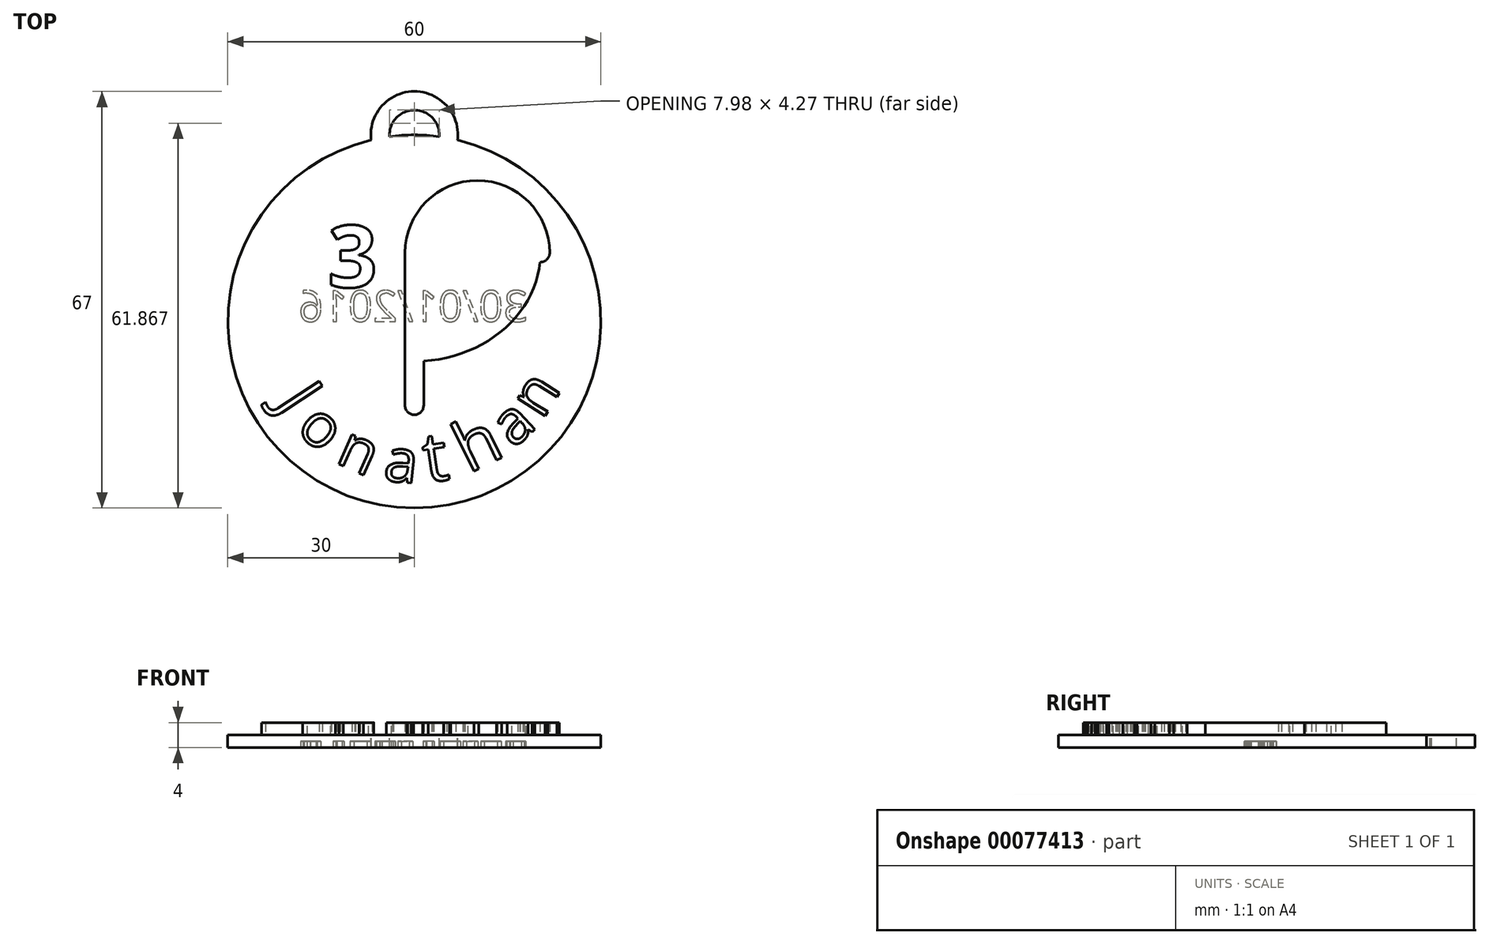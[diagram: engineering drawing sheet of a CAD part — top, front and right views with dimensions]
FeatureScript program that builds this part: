
annotation { "Feature Type Name" : "Feature", "Feature Type Description" : "" }
export const myFeature = defineFeature(function(context is Context, id is Id, definition is map)
    precondition{}
    {
        {
            var Q0;
            Q0=qCreatedBy(makeId("Top.planeOp"),FACE);
            var sketch = newSketch(context, id + "F0", { "sketchPlane" : qUnion([Q0])});
            skCircle(sketch, "E0", {"center": v(0, 0) * mm, "radius": 30 * mm});
            skSolve(sketch);
        }
        {
            var Q0;
            Q0 = qSketchRegion(id + "F0", true);
            extrude(context, id + "F1", {"entities" : qUnion([Q0]), "oppositeDirection" : true, "depth" : 2 * mm});
        }
        {
            var Q0;
            Q0=qCreatedBy(makeId("Top.planeOp"),FACE);
            var sketch = newSketch(context, id + "F2", { "sketchPlane" : qUnion([Q0])});
            skEllipticalArc(sketch, "E1", {});
            skLineSegment(sketch, "E2", {"start": v(0, 0) * mm, "end": v(0, 30) * mm, "construction": true});
            skLineSegment(sketch, "E3", {"start": v(0, 11.04) * mm, "end": v(0, -13.5) * mm});
            skArc(sketch, "E4", {"start": v(20.27, 11.04) * mm, "mid": v(10.13, 21.17) * mm, "end": v(0, 11.04) * mm});
            skLineSegment(sketch, "E5", {"start": v(0, 11.04) * mm, "end": v(-16.84, 20.76) * mm, "construction": true});
            skLineSegment(sketch, "E6", {"start": v(0, 11.04) * mm, "end": v(-20.27, 11.04) * mm, "construction": true});
            skArc(sketch, "E7.0.startCap", {"start": v(-1.5, 11.04) * mm, "mid": v(0, 12.54) * mm, "end": v(1.5, 11.04) * mm});
            skArc(sketch, "E7.0.endCap", {"start": v(1.5, -13.5) * mm, "mid": v(0, -15) * mm, "end": v(-1.5, -13.5) * mm});
            skLineSegment(sketch, "E7.0.left", {"start": v(1.5, 11.04) * mm, "end": v(1.5, -13.5) * mm});
            skLineSegment(sketch, "E7.0.right", {"start": v(-1.5, 11.04) * mm, "end": v(-1.5, -13.5) * mm});
            skArc(sketch, "E8.0.startCap", {"start": v(21.77, 11.04) * mm, "mid": v(20.27, 9.54) * mm, "end": v(18.77, 11.04) * mm});
            skArc(sketch, "E8.0.endCap", {"start": v(1.5, 11.04) * mm, "mid": v(0, 9.54) * mm, "end": v(-1.5, 11.04) * mm});
            skArc(sketch, "E8.0.left", {"start": v(18.77, 11.04) * mm, "mid": v(10.13, 19.67) * mm, "end": v(1.5, 11.04) * mm});
            skArc(sketch, "E8.0.right", {"start": v(21.77, 11.04) * mm, "mid": v(10.13, 22.67) * mm, "end": v(-1.5, 11.04) * mm});
            skArc(sketch, "E8.1.startCap", {"start": v(-18.02, 21.68) * mm, "mid": v(-15.91, 21.95) * mm, "end": v(-15.65, 19.84) * mm});
            skArc(sketch, "E8.1.endCap", {"start": v(18.77, 11.04) * mm, "mid": v(20.27, 12.54) * mm, "end": v(21.77, 11.04) * mm});
            skFitSpline(sketch, "E8.1.left", {"points": [v(18.7, 9.5) * mm, v(18.8, 11.04) * mm, v(18.7, 12.6) * mm, v(18.36, 14.63) * mm, v(17.66, 16.6) * mm, v(16.63, 18.49) * mm, v(15.37, 20.3) * mm, v(13.44, 22.32) * mm, v(11.07, 24) * mm, v(8.94, 25.1) * mm, v(6.7, 26.01) * mm, v(4.32, 26.63) * mm, v(1.87, 26.95) * mm, v(0, 27.03) * mm, v(-1.87, 26.95) * mm, v(-4.32, 26.63) * mm, v(-6.7, 26.01) * mm, v(-8.94, 25.1) * mm, v(-11.07, 24) * mm, v(-13.44, 22.32) * mm, v(-15.37, 20.3) * mm, v(-16.63, 18.49) * mm, v(-17.66, 16.6) * mm, v(-18.36, 14.63) * mm, v(-18.7, 12.6) * mm, v(-18.8, 11.04) * mm, v(-18.7, 9.5) * mm, v(-18.36, 7.46) * mm, v(-17.66, 5.48) * mm, v(-16.63, 3.6) * mm, v(-15.37, 1.8) * mm, v(-13.44, -0.24) * mm, v(-11.07, -1.92) * mm, v(-8.94, -3.02) * mm, v(-6.7, -3.93) * mm, v(-4.32, -4.55) * mm, v(-1.87, -4.86) * mm, v(0, -4.94) * mm, v(1.87, -4.86) * mm, v(4.32, -4.55) * mm, v(6.7, -3.93) * mm, v(8.94, -3.02) * mm, v(11.07, -1.92) * mm, v(13.44, -0.24) * mm, v(15.37, 1.8) * mm, v(16.63, 3.6) * mm, v(17.66, 5.48) * mm, v(18.36, 7.46) * mm, v(18.7, 9.5) * mm, v(18.8, 11.04) * mm, v(18.7, 12.6) * mm]});
            skFitSpline(sketch, "E8.1.right", {"points": [v(21.7, 9.15) * mm, v(21.8, 11.04) * mm, v(21.7, 12.93) * mm, v(21.27, 15.42) * mm, v(20.42, 17.81) * mm, v(19.18, 20.07) * mm, v(17.69, 22.22) * mm, v(15.4, 24.61) * mm, v(12.65, 26.56) * mm, v(10.2, 27.83) * mm, v(7.62, 28.88) * mm, v(4.92, 29.58) * mm, v(2.12, 29.94) * mm, v(0, 30.03) * mm, v(-2.12, 29.94) * mm, v(-4.92, 29.58) * mm, v(-7.62, 28.88) * mm, v(-10.2, 27.83) * mm, v(-12.65, 26.56) * mm, v(-15.4, 24.61) * mm, v(-17.69, 22.22) * mm, v(-19.18, 20.07) * mm, v(-20.42, 17.81) * mm, v(-21.27, 15.42) * mm, v(-21.7, 12.93) * mm, v(-21.8, 11.04) * mm, v(-21.7, 9.15) * mm, v(-21.27, 6.67) * mm, v(-20.42, 4.27) * mm, v(-19.18, 2) * mm, v(-17.69, -0.14) * mm, v(-15.4, -2.53) * mm, v(-12.65, -4.48) * mm, v(-10.2, -5.75) * mm, v(-7.62, -6.8) * mm, v(-4.92, -7.5) * mm, v(-2.12, -7.86) * mm, v(0, -7.95) * mm, v(2.12, -7.86) * mm, v(4.92, -7.5) * mm, v(7.62, -6.8) * mm, v(10.2, -5.75) * mm, v(12.65, -4.48) * mm, v(15.4, -2.53) * mm, v(17.69, -0.14) * mm, v(19.18, 2) * mm, v(20.42, 4.27) * mm, v(21.27, 6.67) * mm, v(21.7, 9.15) * mm, v(21.8, 11.04) * mm, v(21.7, 12.93) * mm]});
            const initialGuessF2  = {"E1": [0, 0.011041626236194823, 1, 0, 0.020266667008310185, 0.017458373763805178, 2.5511335140588507, 0]};
            skSetInitialGuess(sketch, initialGuessF2);
            skSolve(sketch);
        }
        {
            var Q0;
            {var subQ0=sQuery(id+"F2.wireOp",EDGE,"E8.1.startCap");Q0=makeQuery(id+"F2.imprint","IMPRINT",FACE,{"disambiguationData":[TD([[makeQuery(id+"F2.imprint","IMPRINT",EDGE,{"derivedFrom":subQ0}),-1.0]])]});}
            var Q1;
            {var subQ0=sQuery(id+"F2.wireOp",EDGE,"E7.0.right");var subQ1=sQuery(id+"F2.wireOp",EDGE,"E1");var subQ2=makeQuery(id+"F2.imprint","INTERSECT",VERTEX,{"derivedFrom":[subQ1,subQ0]});Q1=makeQuery(id+"F2.imprint","IMPRINT",FACE,{"disambiguationData":[TD([[makeQuery(id+"F2.imprint","IMPRINT",EDGE,{"disambiguationData":[TD([[subQ2,-1.0]])],"derivedFrom":subQ1}),1.0]])]});}
            var Q2;
            {var subQ0=sQuery(id+"F2.wireOp",EDGE,"E3");var subQ1=sQuery(id+"F2.wireOp",EDGE,"E1");var subQ2=makeQuery(id+"F2.imprint","INTERSECT",VERTEX,{"derivedFrom":[subQ1,subQ0]});Q2=makeQuery(id+"F2.imprint","IMPRINT",FACE,{"disambiguationData":[TD([[makeQuery(id+"F2.imprint","IMPRINT",EDGE,{"disambiguationData":[TD([[subQ2,-1.0]])],"derivedFrom":subQ1}),1.0]])]});}
            var Q3;
            {var subQ0=sQuery(id+"F2.wireOp",EDGE,"E7.0.right");var subQ1=sQuery(id+"F2.wireOp",EDGE,"E1");var subQ2=makeQuery(id+"F2.imprint","INTERSECT",VERTEX,{"derivedFrom":[subQ1,subQ0]});Q3=makeQuery(id+"F2.imprint","IMPRINT",FACE,{"disambiguationData":[TD([[makeQuery(id+"F2.imprint","IMPRINT",EDGE,{"disambiguationData":[TD([[subQ2,-1.0]])],"derivedFrom":subQ1}),-1.0]])]});}
            var Q4;
            {var subQ0=sQuery(id+"F2.wireOp",EDGE,"E3");var subQ1=sQuery(id+"F2.wireOp",EDGE,"E1");var subQ2=makeQuery(id+"F2.imprint","INTERSECT",VERTEX,{"derivedFrom":[subQ1,subQ0]});Q4=makeQuery(id+"F2.imprint","IMPRINT",FACE,{"disambiguationData":[TD([[makeQuery(id+"F2.imprint","IMPRINT",EDGE,{"disambiguationData":[TD([[subQ2,-1.0]])],"derivedFrom":subQ1}),-1.0]])]});}
            var Q5;
            {var subQ0=sQuery(id+"F2.wireOp",EDGE,"E7.0.left");var subQ1=sQuery(id+"F2.wireOp",EDGE,"E1");var subQ2=makeQuery(id+"F2.imprint","INTERSECT",VERTEX,{"derivedFrom":[subQ1,subQ0]});Q5=makeQuery(id+"F2.imprint","IMPRINT",FACE,{"disambiguationData":[TD([[makeQuery(id+"F2.imprint","IMPRINT",EDGE,{"disambiguationData":[TD([[subQ2,-1.0]])],"derivedFrom":subQ1}),-1.0]])]});}
            var Q6;
            {var subQ0=sQuery(id+"F2.wireOp",EDGE,"E7.0.left");var subQ1=sQuery(id+"F2.wireOp",EDGE,"E1");var subQ2=makeQuery(id+"F2.imprint","INTERSECT",VERTEX,{"derivedFrom":[subQ1,subQ0]});Q6=makeQuery(id+"F2.imprint","IMPRINT",FACE,{"disambiguationData":[TD([[makeQuery(id+"F2.imprint","IMPRINT",EDGE,{"disambiguationData":[TD([[subQ2,-1.0]])],"derivedFrom":subQ1}),1.0]])]});}
            var Q7;
            {var subQ0=sQuery(id+"F2.wireOp",EDGE,"E4");var subQ1=sQuery(id+"F2.wireOp",EDGE,"E1");var subQ2=makeQuery(id+"F2.imprint","INTERSECT",VERTEX,{"derivedFrom":[subQ1,subQ0]});Q7=makeQuery(id+"F2.imprint","IMPRINT",FACE,{"disambiguationData":[TD([[makeQuery(id+"F2.imprint","IMPRINT",EDGE,{"disambiguationData":[TD([[subQ2,1.0]])],"derivedFrom":subQ1}),-1.0]])]});}
            var Q8;
            {var subQ0=sQuery(id+"F2.wireOp",EDGE,"E4");var subQ1=sQuery(id+"F2.wireOp",EDGE,"E1");var subQ2=makeQuery(id+"F2.imprint","INTERSECT",VERTEX,{"derivedFrom":[subQ1,subQ0]});Q8=makeQuery(id+"F2.imprint","IMPRINT",FACE,{"disambiguationData":[TD([[makeQuery(id+"F2.imprint","IMPRINT",EDGE,{"disambiguationData":[TD([[subQ2,1.0]])],"derivedFrom":subQ1}),1.0]])]});}
            var Q9;
            {var subQ5=sQuery(id+"F2.wireOp",EDGE,"E8.0.left");Q9=makeQuery(id+"F2.imprint","IMPRINT",FACE,{"disambiguationData":[TD([[makeQuery(id+"F2.imprint","IMPRINT",EDGE,{"derivedFrom":subQ5}),-1.0]])]});}
            var Q10;
            {var subQ5=sQuery(id+"F2.wireOp",EDGE,"E8.0.right");Q10=makeQuery(id+"F2.imprint","IMPRINT",FACE,{"disambiguationData":[TD([[makeQuery(id+"F2.imprint","IMPRINT",EDGE,{"derivedFrom":subQ5}),1.0]])]});}
            var Q11;
            {var subQ0=sQuery(id+"F2.wireOp",EDGE,"E4");var subQ1=sQuery(id+"F2.wireOp",EDGE,"E3");var subQ2=makeQuery(id+"F2.imprint","INTERSECT",VERTEX,{"derivedFrom":[subQ1,subQ0]});Q11=makeQuery(id+"F2.imprint","IMPRINT",FACE,{"disambiguationData":[TD([[makeQuery(id+"F2.imprint","IMPRINT",EDGE,{"disambiguationData":[TD([[subQ2,-1.0]])],"derivedFrom":subQ1}),-1.0]])]});}
            var Q12;
            {var subQ0=sQuery(id+"F2.wireOp",EDGE,"E4");var subQ1=sQuery(id+"F2.wireOp",EDGE,"E3");var subQ2=makeQuery(id+"F2.imprint","INTERSECT",VERTEX,{"derivedFrom":[subQ1,subQ0]});Q12=makeQuery(id+"F2.imprint","IMPRINT",FACE,{"disambiguationData":[TD([[makeQuery(id+"F2.imprint","IMPRINT",EDGE,{"disambiguationData":[TD([[subQ2,-1.0]])],"derivedFrom":subQ1}),1.0]])]});}
            var Q13;
            {var subQ0=sQuery(id+"F2.wireOp",EDGE,"E8.0.endCap");var subQ1=sQuery(id+"F2.wireOp",EDGE,"E3");var subQ2=makeQuery(id+"F2.imprint","INTERSECT",VERTEX,{"derivedFrom":[subQ1,subQ0]});Q13=makeQuery(id+"F2.imprint","IMPRINT",FACE,{"disambiguationData":[TD([[makeQuery(id+"F2.imprint","IMPRINT",EDGE,{"disambiguationData":[TD([[subQ2,-1.0]])],"derivedFrom":subQ1}),-1.0]])]});}
            var Q14;
            {var subQ0=sQuery(id+"F2.wireOp",EDGE,"E8.0.endCap");var subQ1=sQuery(id+"F2.wireOp",EDGE,"E3");var subQ2=makeQuery(id+"F2.imprint","INTERSECT",VERTEX,{"derivedFrom":[subQ1,subQ0]});Q14=makeQuery(id+"F2.imprint","IMPRINT",FACE,{"disambiguationData":[TD([[makeQuery(id+"F2.imprint","IMPRINT",EDGE,{"disambiguationData":[TD([[subQ2,-1.0]])],"derivedFrom":subQ1}),1.0]])]});}
            var Q15;
            {var subQ1=sQuery(id+"F2.wireOp",EDGE,"E7.0.endCap");Q15=makeQuery(id+"F2.imprint","IMPRINT",FACE,{"disambiguationData":[TD([[makeQuery(id+"F2.imprint","IMPRINT",EDGE,{"derivedFrom":subQ1}),-1.0]])]});}
            extrude(context, id + "F3", {"entities" : qUnion([Q0, Q1, Q2, Q3, Q4, Q5, Q6, Q7, Q8, Q9, Q10, Q11, Q12, Q13, Q14, Q15]), "operationType" : NewBodyOperationType.ADD, "depth" : 2 * mm});
        }
        {
            var Q0;
            Q0=qCreatedBy(makeId("Top.planeOp"),FACE);
            var sketch = newSketch(context, id + "F4", { "sketchPlane" : qUnion([Q0])});
            skText(sketch, "E9", { "text": "3", "fontName": "OpenSans-Bold.ttf"});
            skText(sketch, "E10", { "text": "D", "fontName": "OpenSans-Bold.ttf"});
            const initialGuessF4  = {"E9": [-0.0139, 0.0055, 1, 0, 0.01], "E10": [0.0055, 0.0055, 1, 0, 0.01]};
            skSetInitialGuess(sketch, initialGuessF4);
            skSolve(sketch);
        }
        {
            var Q0;
            Q0 = qSketchRegion(id + "F4", true);
            extrude(context, id + "F5", {"entities" : qUnion([Q0]), "operationType" : NewBodyOperationType.ADD, "depth" : 2 * mm});
        }
        {
            var Q0;
            {var subQ8=sQuery(id+"F0.wireOp",EDGE,"E0");Q0=makeQuery(id+"F3.boolean.opBoolean","SPLIT",FACE,{"disambiguationData":[TD([makeQuery(id+"F1.opExtrude","SWEPT_FACE",FACE,{"disambiguationData":[OSD([subQ8])]})])],"derivedFrom":makeQuery(id+"F1.opExtrude","CAP_FACE",FACE,{"disambiguationData":[OSD([subQ8])],"isStart":true})});}
            var sketch = newSketch(context, id + "F6", { "sketchPlane" : qUnion([Q0])});
            skCircle(sketch, "E11.0", {"center": v(0, 0) * mm, "radius": 26 * mm, "construction": true});
            skText(sketch, "E12", { "text": "J", "fontName": "OpenSans-Regular.ttf"});
            skText(sketch, "E13", { "text": "o", "fontName": "OpenSans-Regular.ttf"});
            skText(sketch, "E14", { "text": "n", "fontName": "OpenSans-Regular.ttf"});
            skText(sketch, "E15", { "text": "a", "fontName": "OpenSans-Regular.ttf"});
            skText(sketch, "E16", { "text": "t", "fontName": "OpenSans-Regular.ttf"});
            skText(sketch, "E17", { "text": "h", "fontName": "OpenSans-Regular.ttf"});
            skText(sketch, "E18", { "text": "a", "fontName": "OpenSans-Regular.ttf"});
            skText(sketch, "E19", { "text": "n", "fontName": "OpenSans-Regular.ttf"});
            const initialGuessF6  = {"E12": [-0.02247, -0.01307, 0.54895, -0.83585, 0.008], "E13": [-0.01926, -0.01747, 0.74423, -0.66792, 0.007], "E14": [-0.0129, -0.02257, 0.91323, -0.40744, 0.007], "E15": [-0.00512, -0.0255, 0.99403, -0.10907, 0.007], "E16": [0.002, -0.02592, 0.98901, 0.14783, 0.008], "E17": [0.00872, -0.0245, 0.89777, 0.44047, 0.008], "E18": [0.01598, -0.02051, 0.73125, 0.68211, 0.007], "E19": [0.02059, -0.01588, 0.52886, 0.8487, 0.007]};
            skSetInitialGuess(sketch, initialGuessF6);
            skSolve(sketch);
        }
        {
            var Q0;
            Q0 = qSketchRegion(id + "F6", true);
            extrude(context, id + "F7", {"entities" : qUnion([Q0]), "operationType" : NewBodyOperationType.ADD, "depth" : 2 * mm});
        }
        {
            var Q0;
            Q0=qCreatedBy(makeId("Top.planeOp"),FACE);
            var sketch = newSketch(context, id + "F8", { "sketchPlane" : qUnion([Q0])});
            skArc(sketch, "E20", {"start": v(5.48, 29.5) * mm, "mid": v(0, 35.5) * mm, "end": v(-5.48, 29.5) * mm});
            skArc(sketch, "E21.0.startCap", {"start": v(6.97, 29.36) * mm, "mid": v(5.34, 28) * mm, "end": v(3.98, 29.63) * mm});
            skArc(sketch, "E21.0.endCap", {"start": v(-3.98, 29.63) * mm, "mid": v(-5.34, 28) * mm, "end": v(-6.97, 29.36) * mm});
            skArc(sketch, "E21.0.left", {"start": v(3.98, 29.63) * mm, "mid": v(0, 34) * mm, "end": v(-3.98, 29.63) * mm});
            skArc(sketch, "E21.0.right", {"start": v(6.97, 29.36) * mm, "mid": v(0, 37) * mm, "end": v(-6.97, 29.36) * mm});
            skSolve(sketch);
        }
        {
            var Q0;
            Q0 = qSketchRegion(id + "F8", true);
            extrude(context, id + "F9", {"entities" : qUnion([Q0]), "operationType" : NewBodyOperationType.ADD, "oppositeDirection" : true, "depth" : 2 * mm});
        }
        {
            var Q0;
            Q0=makeQuery(id+"F9.boolean.opBoolean","MERGE",FACE,{"derivedFrom":[makeQuery(id+"F1.opExtrude","CAP_FACE",FACE,{"disambiguationData":[OSD([sQuery(id+"F0.wireOp",EDGE,"E0")])],"isStart":false}),makeQuery(id+"F9.opExtrude","CAP_FACE",FACE,{"disambiguationData":[OSD([sQuery(id+"F8.wireOp",EDGE,"E21.0.startCap"),sQuery(id+"F8.wireOp",EDGE,"E21.0.endCap"),sQuery(id+"F8.wireOp",EDGE,"E21.0.left"),sQuery(id+"F8.wireOp",EDGE,"E21.0.right")])],"isStart":false})]});
            var sketch = newSketch(context, id + "F10", { "sketchPlane" : qUnion([Q0])});
            skText(sketch, "E22", { "text": "30/01/2016", "fontName": "OpenSans-Regular.ttf"});
            const initialGuessF10  = {"E22": [0.01826, 0, -1, 0, 0.005]};
            skSetInitialGuess(sketch, initialGuessF10);
            skSolve(sketch);
        }
        {
            var Q0;
            Q0 = qSketchRegion(id + "F10", true);
            extrude(context, id + "F11", {"entities" : qUnion([Q0]), "operationType" : NewBodyOperationType.REMOVE, "oppositeDirection" : true, "depth" : 1 * mm});
        }
    });
